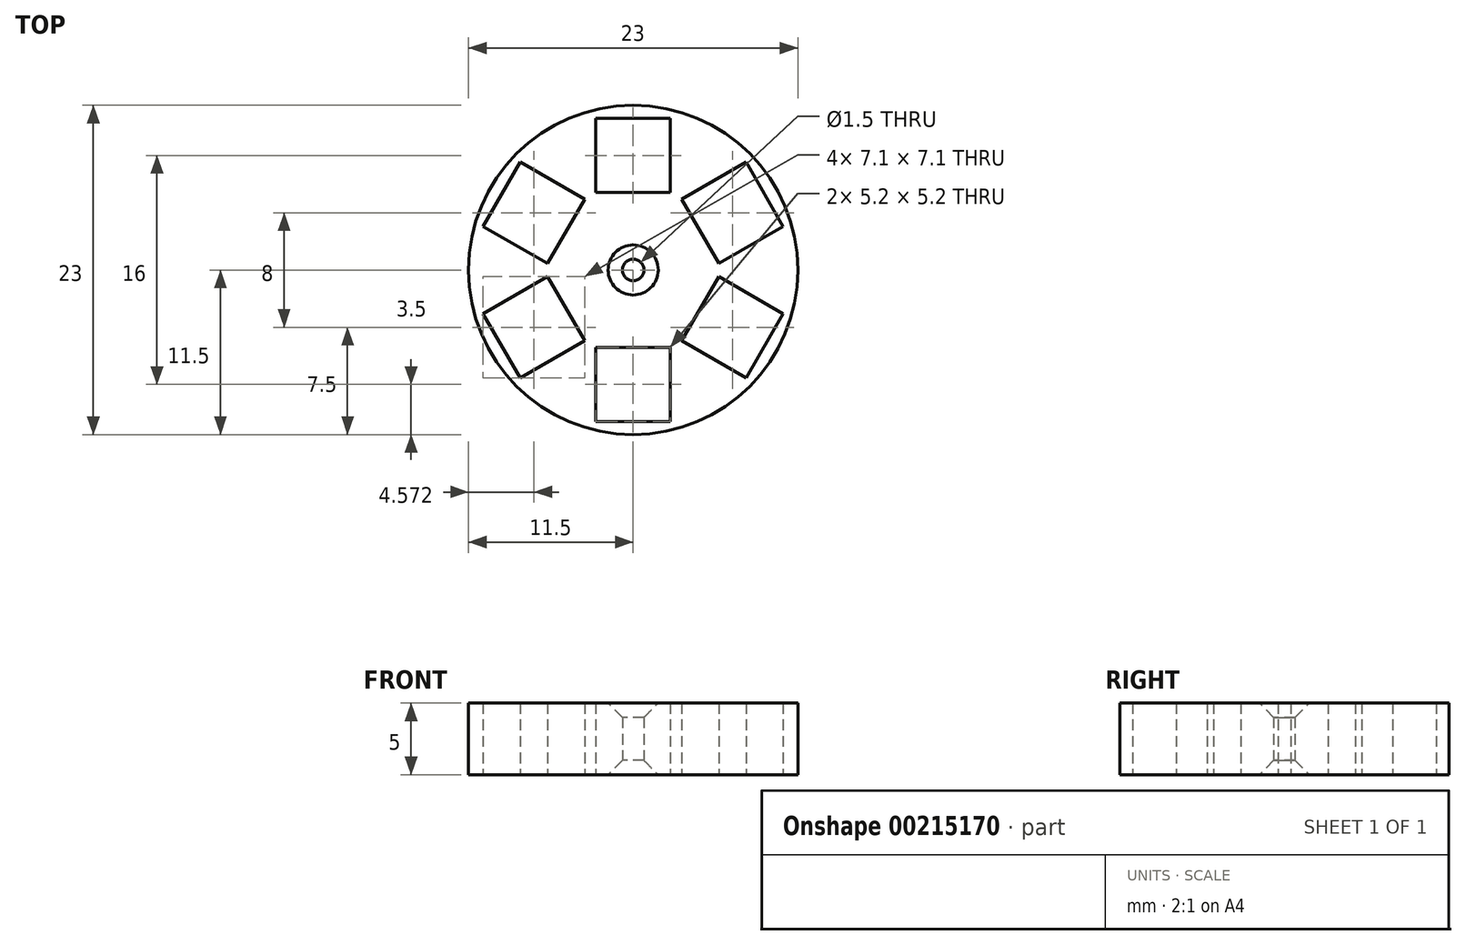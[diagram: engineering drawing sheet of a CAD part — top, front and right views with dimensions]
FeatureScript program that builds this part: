
annotation { "Feature Type Name" : "Feature", "Feature Type Description" : "" }
export const myFeature = defineFeature(function(context is Context, id is Id, definition is map)
    precondition{}
    {
        {
            var Q0;
            Q0=qCreatedBy(makeId("Top.planeOp"),FACE);
            var sketch = newSketch(context, id + "F0", { "sketchPlane" : qUnion([Q0])});
            skCircle(sketch, "E0", {"center": v(0, 0) * mm, "radius": 11.5 * mm});
            skCircle(sketch, "E1", {"center": v(0, 0) * mm, "radius": 0.75 * mm});
            skLineSegment(sketch, "E2.bottom", {"start": v(2.6, 10.6) * mm, "end": v(-2.6, 10.6) * mm});
            skLineSegment(sketch, "E2.top", {"start": v(2.6, 5.4) * mm, "end": v(-2.6, 5.4) * mm});
            skLineSegment(sketch, "E2.left", {"start": v(2.6, 10.6) * mm, "end": v(2.6, 5.4) * mm});
            skLineSegment(sketch, "E2.right", {"start": v(-2.6, 10.6) * mm, "end": v(-2.6, 5.4) * mm});
            skPoint(sketch, "E2.middle", {"position": v(0, 8) * mm});
            skLineSegment(sketch, "E3.1.0", {"start": v(-7.88, 7.55) * mm, "end": v(-10.48, 3.05) * mm});
            skLineSegment(sketch, "E3.1.1", {"start": v(-7.88, 7.55) * mm, "end": v(-3.38, 4.95) * mm});
            skLineSegment(sketch, "E3.1.2", {"start": v(-3.38, 4.95) * mm, "end": v(-5.98, 0.45) * mm});
            skLineSegment(sketch, "E3.1.3", {"start": v(-10.48, 3.05) * mm, "end": v(-5.98, 0.45) * mm});
            skPoint(sketch, "E3.1.4", {"position": v(-6.93, 4) * mm});
            skLineSegment(sketch, "E3.2.0", {"start": v(-10.48, -3.05) * mm, "end": v(-7.88, -7.55) * mm});
            skLineSegment(sketch, "E3.2.1", {"start": v(-10.48, -3.05) * mm, "end": v(-5.98, -0.45) * mm});
            skLineSegment(sketch, "E3.2.2", {"start": v(-5.98, -0.45) * mm, "end": v(-3.38, -4.95) * mm});
            skLineSegment(sketch, "E3.2.3", {"start": v(-7.88, -7.55) * mm, "end": v(-3.38, -4.95) * mm});
            skPoint(sketch, "E3.2.4", {"position": v(-6.93, -4) * mm});
            skLineSegment(sketch, "E3.3.0", {"start": v(-2.6, -10.6) * mm, "end": v(2.6, -10.6) * mm});
            skLineSegment(sketch, "E3.3.1", {"start": v(-2.6, -10.6) * mm, "end": v(-2.6, -5.4) * mm});
            skLineSegment(sketch, "E3.3.2", {"start": v(-2.6, -5.4) * mm, "end": v(2.6, -5.4) * mm});
            skLineSegment(sketch, "E3.3.3", {"start": v(2.6, -10.6) * mm, "end": v(2.6, -5.4) * mm});
            skPoint(sketch, "E3.3.4", {"position": v(0, -8) * mm});
            skLineSegment(sketch, "E3.4.0", {"start": v(7.88, -7.55) * mm, "end": v(10.48, -3.05) * mm});
            skLineSegment(sketch, "E3.4.1", {"start": v(7.88, -7.55) * mm, "end": v(3.38, -4.95) * mm});
            skLineSegment(sketch, "E3.4.2", {"start": v(3.38, -4.95) * mm, "end": v(5.98, -0.45) * mm});
            skLineSegment(sketch, "E3.4.3", {"start": v(10.48, -3.05) * mm, "end": v(5.98, -0.45) * mm});
            skPoint(sketch, "E3.4.4", {"position": v(6.93, -4) * mm});
            skLineSegment(sketch, "E3.5.0", {"start": v(10.48, 3.05) * mm, "end": v(7.88, 7.55) * mm});
            skLineSegment(sketch, "E3.5.1", {"start": v(10.48, 3.05) * mm, "end": v(5.98, 0.45) * mm});
            skLineSegment(sketch, "E3.5.2", {"start": v(5.98, 0.45) * mm, "end": v(3.38, 4.95) * mm});
            skLineSegment(sketch, "E3.5.3", {"start": v(7.88, 7.55) * mm, "end": v(3.38, 4.95) * mm});
            skPoint(sketch, "E3.5.4", {"position": v(6.93, 4) * mm});
            skSolve(sketch);
        }
        {
            var Q0;
            Q0=makeQuery(id+"F0.imprint","IMPRINT",FACE,{"disambiguationData":[TD([[makeQuery(id+"F0.imprint","IMPRINT",EDGE,{"derivedFrom":sQuery(id+"F0.wireOp",EDGE,"E0")}),1.0]])]});
            extrude(context, id + "F1", {"entities" : qUnion([Q0]), "depth" : 5 * mm});
        }
        {
            var Q0;
            Q0=makeQuery(id+"F1.opExtrude","CAP_EDGE",EDGE,{"disambiguationData":[OSD([sQuery(id+"F0.wireOp",EDGE,"E1")])],"isStart":false});
            var Q1;
            Q1=makeQuery(id+"F1.opExtrude","CAP_EDGE",EDGE,{"disambiguationData":[OSD([sQuery(id+"F0.wireOp",EDGE,"E1")])],"isStart":true});
            chamfer(context, id + "F2", {"entities" : qUnion([Q0, Q1]), "width" : 1 * mm, "tangentPropagation" : true});
        }
    });
